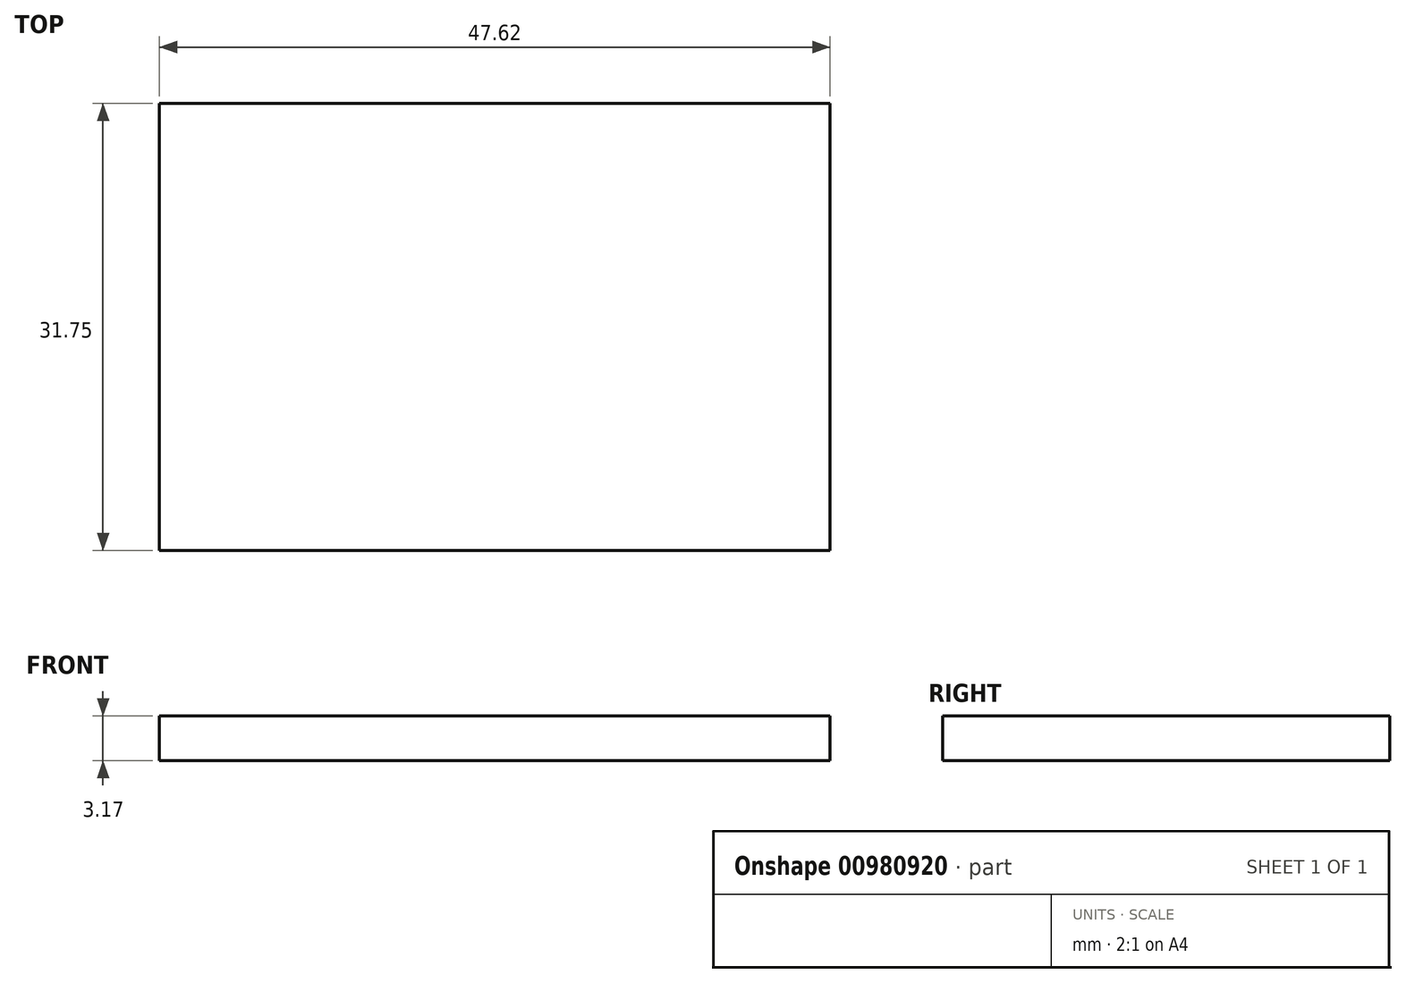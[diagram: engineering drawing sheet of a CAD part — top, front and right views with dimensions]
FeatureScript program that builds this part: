
annotation { "Feature Type Name" : "Feature", "Feature Type Description" : "" }
export const myFeature = defineFeature(function(context is Context, id is Id, definition is map)
    precondition{}
    {
        {
            var Q0;
            Q0=qCreatedBy(makeId("Top.planeOp"),FACE);
            var sketch = newSketch(context, id + "F0", { "sketchPlane" : qUnion([Q0])});
            skLineSegment(sketch, "E0.bottom", {"start": v(0, 0) * mm, "end": v(-47.63, 0) * mm});
            skLineSegment(sketch, "E0.top", {"start": v(0, 31.75) * mm, "end": v(-47.63, 31.75) * mm});
            skLineSegment(sketch, "E0.left", {"start": v(0, 0) * mm, "end": v(0, 31.75) * mm});
            skLineSegment(sketch, "E0.right", {"start": v(-47.63, 0) * mm, "end": v(-47.63, 31.75) * mm});
            skSolve(sketch);
        }
        {
            var Q0;
            Q0 = qSketchRegion(id + "F0", true);
            extrude(context, id + "F1", {"entities" : qUnion([Q0]), "depth" : 3.17 * mm, "offsetDistance" : 25.4 * mm});
        }
    });
